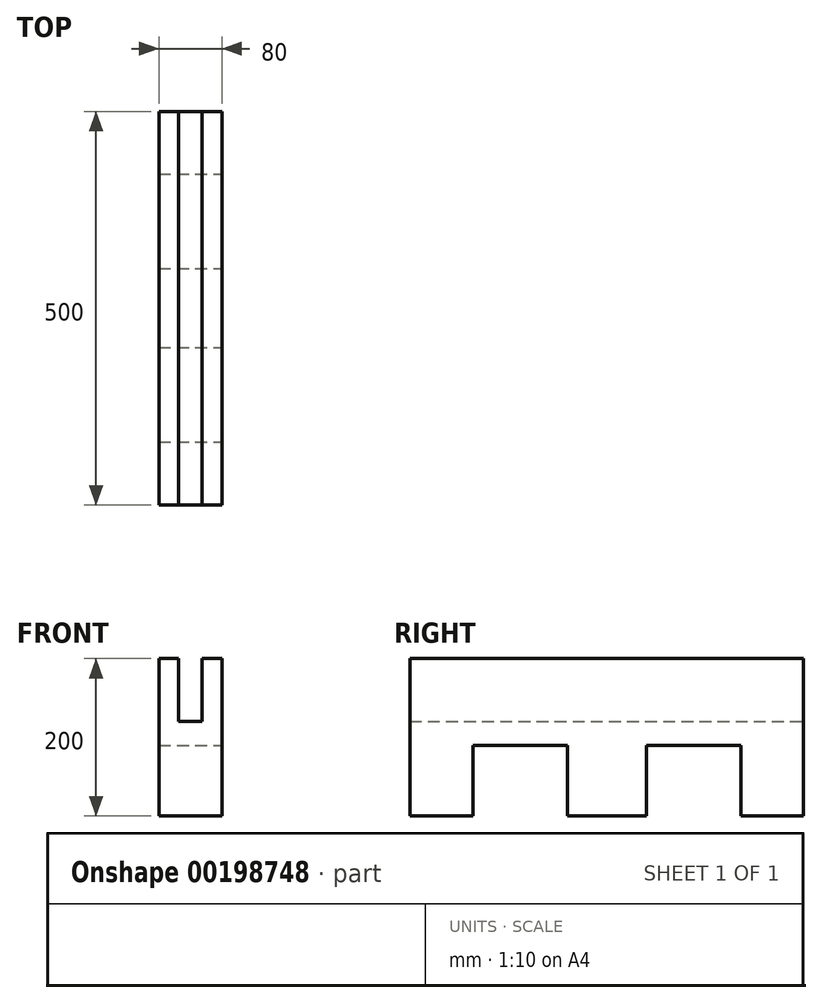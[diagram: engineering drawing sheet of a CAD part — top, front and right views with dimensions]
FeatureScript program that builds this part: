
annotation { "Feature Type Name" : "Feature", "Feature Type Description" : "" }
export const myFeature = defineFeature(function(context is Context, id is Id, definition is map)
    precondition{}
    {
        {
            var Q0;
            Q0=qCreatedBy(makeId("Front.planeOp"),FACE);
            var sketch = newSketch(context, id + "F0", { "sketchPlane" : qUnion([Q0])});
            skLineSegment(sketch, "E0.right", {"start": v(40, 0) * mm, "end": v(40, 120) * mm});
            skLineSegment(sketch, "E1.top", {"start": v(-40, 200) * mm, "end": v(-15, 200) * mm});
            skLineSegment(sketch, "E1.left", {"start": v(-40, 120) * mm, "end": v(-40, 200) * mm});
            skLineSegment(sketch, "E1.right", {"start": v(-15, 120) * mm, "end": v(-15, 200) * mm});
            skLineSegment(sketch, "E2.top", {"start": v(40, 200) * mm, "end": v(15, 200) * mm});
            skLineSegment(sketch, "E2.left", {"start": v(40, 120) * mm, "end": v(40, 200) * mm});
            skLineSegment(sketch, "E2.right", {"start": v(15, 120) * mm, "end": v(15, 200) * mm});
            skPoint(sketch, "E3", {"position": v(0, 120) * mm});
            skLineSegment(sketch, "E4", {"start": v(-40, 120) * mm, "end": v(-40, 0) * mm});
            skLineSegment(sketch, "E5", {"start": v(-40, 0) * mm, "end": v(40, 0) * mm});
            skLineSegment(sketch, "E6", {"start": v(-15, 120) * mm, "end": v(15, 120) * mm});
            skSolve(sketch);
        }
        {
            var Q0;
            Q0 = qSketchRegion(id + "F0", true);
            extrude(context, id + "F1", {"entities" : qUnion([Q0]), "endBound" : BoundingType.SYMMETRIC, "depth" : 500 * mm});
        }
        {
            var Q0;
            Q0=makeQuery(id+"F1.opExtrude","SWEPT_FACE",FACE,{"disambiguationData":[OSD([sQuery(id+"F0.wireOp",EDGE,"E0.right"),sQuery(id+"F0.wireOp",EDGE,"E2.left")])]});
            var sketch = newSketch(context, id + "F2", { "sketchPlane" : qUnion([Q0])});
            skLineSegment(sketch, "E7.right", {"start": v(-170, 0) * mm, "end": v(-170, 72.96) * mm});
            skLineSegment(sketch, "E8.bottom", {"start": v(-170, 0) * mm, "end": v(-50, 0) * mm});
            skLineSegment(sketch, "E8.top", {"start": v(-170, 90) * mm, "end": v(-50, 90) * mm});
            skLineSegment(sketch, "E8.left", {"start": v(-170, 0) * mm, "end": v(-170, 90) * mm});
            skLineSegment(sketch, "E8.right", {"start": v(-50, 0) * mm, "end": v(-50, 90) * mm});
            skLineSegment(sketch, "E9.right", {"start": v(170.59, 0) * mm, "end": v(170.59, 72.96) * mm});
            skLineSegment(sketch, "E10.bottom", {"start": v(170.59, 0) * mm, "end": v(50.59, 0) * mm});
            skLineSegment(sketch, "E10.top", {"start": v(170.59, 90) * mm, "end": v(50.59, 90) * mm});
            skLineSegment(sketch, "E10.left", {"start": v(170.59, 0) * mm, "end": v(170.59, 90) * mm});
            skLineSegment(sketch, "E10.right", {"start": v(50.59, 0) * mm, "end": v(50.59, 90) * mm});
            skSolve(sketch);
        }
        {
            var Q0;
            Q0 = qSketchRegion(id + "F2", true);
            extrude(context, id + "F3", {"entities" : qUnion([Q0]), "operationType" : NewBodyOperationType.REMOVE, "endBound" : BoundingType.THROUGH_ALL, "oppositeDirection" : true, "depth" : 25 * mm});
        }
    });
